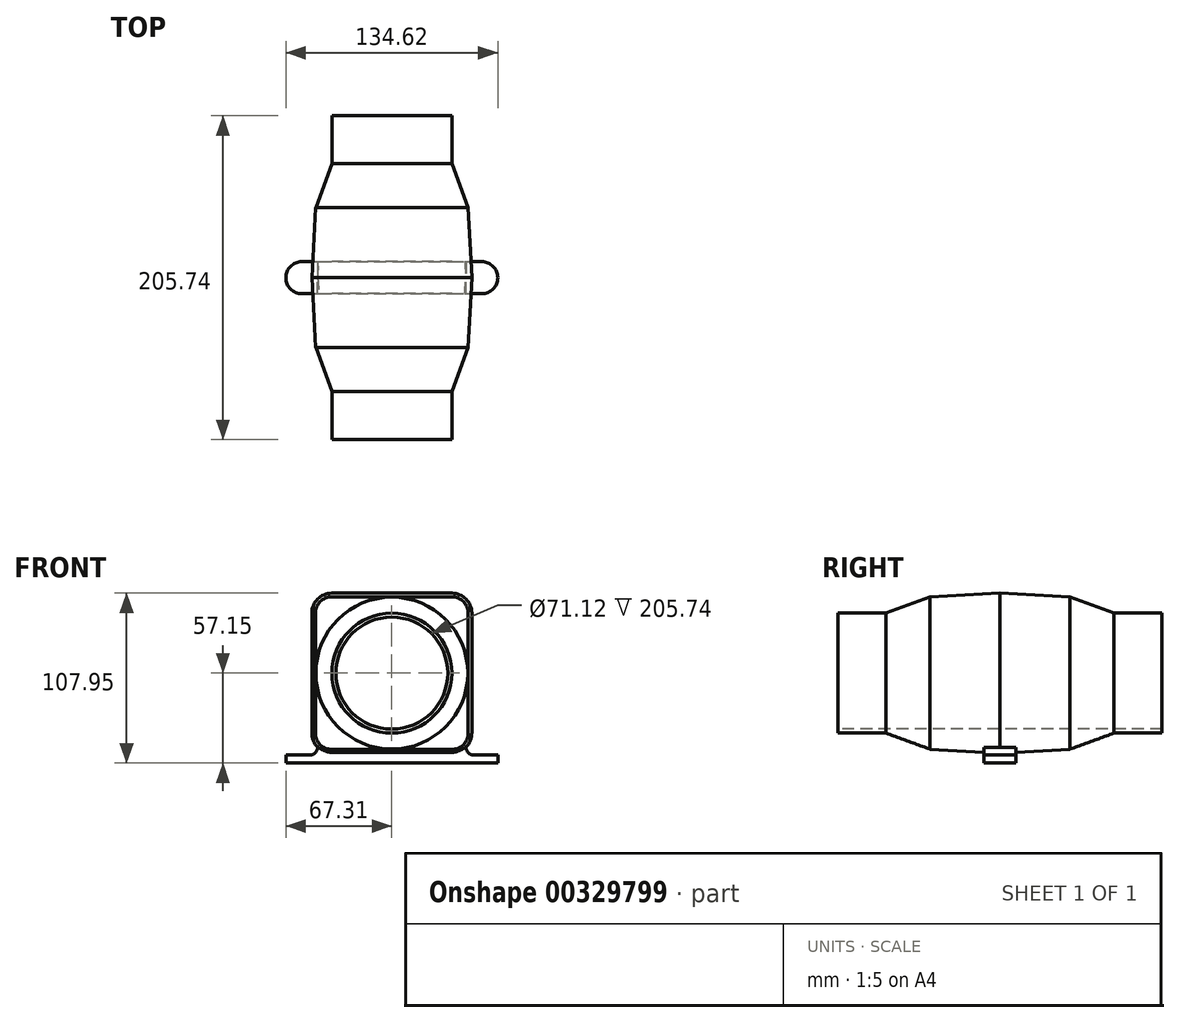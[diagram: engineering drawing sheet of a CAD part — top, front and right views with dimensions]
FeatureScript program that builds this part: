
annotation { "Feature Type Name" : "Feature", "Feature Type Description" : "" }
export const myFeature = defineFeature(function(context is Context, id is Id, definition is map)
    precondition{}
    {
        {
            var Q0;
            Q0=qCreatedBy(makeId("Front.planeOp"),FACE);
            var sketch = newSketch(context, id + "F0", { "sketchPlane" : qUnion([Q0])});
            skLineSegment(sketch, "E0.bottom", {"start": v(38.1, -50.8) * mm, "end": v(-38.1, -50.8) * mm});
            skLineSegment(sketch, "E0.top", {"start": v(38.1, 50.8) * mm, "end": v(-38.1, 50.8) * mm});
            skLineSegment(sketch, "E0.left", {"start": v(50.8, -38.1) * mm, "end": v(50.8, 38.1) * mm});
            skLineSegment(sketch, "E0.right", {"start": v(-50.8, -38.1) * mm, "end": v(-50.8, 38.1) * mm});
            skPoint(sketch, "E0.middle", {"position": v(0, 0) * mm});
            skPoint(sketch, "E1.visualSharp", {"position": v(50.8, 50.8) * mm});
            skArc(sketch, "E1.filletArc", {"start": v(50.8, 38.1) * mm, "mid": v(47.08, 47.08) * mm, "end": v(38.1, 50.8) * mm});
            skPoint(sketch, "E2.visualSharp", {"position": v(-50.8, 50.8) * mm});
            skArc(sketch, "E2.filletArc", {"start": v(-38.1, 50.8) * mm, "mid": v(-47.08, 47.08) * mm, "end": v(-50.8, 38.1) * mm});
            skPoint(sketch, "E3.visualSharp", {"position": v(-50.8, -50.8) * mm});
            skArc(sketch, "E3.filletArc", {"start": v(-50.8, -38.1) * mm, "mid": v(-47.08, -47.08) * mm, "end": v(-38.1, -50.8) * mm});
            skPoint(sketch, "E4.visualSharp", {"position": v(50.8, -50.8) * mm});
            skArc(sketch, "E4.filletArc", {"start": v(38.1, -50.8) * mm, "mid": v(47.08, -47.08) * mm, "end": v(50.8, -38.1) * mm});
            skSolve(sketch);
        }
        {
            var Q0;
            Q0=qSketchRegion(id+"F0",true);
            extrude(context, id + "F1", {"entities" : qUnion([Q0]), "depth" : 44.45 * mm, "hasDraft" : true, "draftAngle" : 3 * degree, "draftPullDirection" : true, "hasSecondDirectionDraft" : true, "secondDirectionDraftAngle" : 3 * degree, "secondDirectionDraftPullDirection" : true});
        }
        {
            var Q0;
            Q0=makeQuery(id+"F1.opExtrude","CAP_FACE",FACE,{"disambiguationData":[OSD([sQuery(id+"F0.wireOp",EDGE,"E0.bottom"),sQuery(id+"F0.wireOp",EDGE,"E0.top"),sQuery(id+"F0.wireOp",EDGE,"E0.left"),sQuery(id+"F0.wireOp",EDGE,"E0.right"),sQuery(id+"F0.wireOp",EDGE,"E1.filletArc"),sQuery(id+"F0.wireOp",EDGE,"E2.filletArc"),sQuery(id+"F0.wireOp",EDGE,"E3.filletArc"),sQuery(id+"F0.wireOp",EDGE,"E4.filletArc")])],"isStart":false});
            var sketch = newSketch(context, id + "F2", { "sketchPlane" : qUnion([Q0])});
            skCircle(sketch, "E5", {"center": v(0, 0) * mm, "radius": 48.26 * mm});
            skSolve(sketch);
        }
        {
            var Q0;
            Q0=qSketchRegion(id+"F2",true);
            extrude(context, id + "F3", {"entities" : qUnion([Q0]), "operationType" : NewBodyOperationType.ADD, "depth" : 27.94 * mm, "hasDraft" : true, "draftAngle" : 20 * degree, "draftPullDirection" : true});
        }
        {
            var Q0;
            Q0=makeQuery(id+"F3.opExtrude","CAP_FACE",FACE,{"disambiguationData":[OSD([sQuery(id+"F2.wireOp",EDGE,"E5")])],"isStart":false});
            var sketch = newSketch(context, id + "F4", { "sketchPlane" : qUnion([Q0])});
            skCircle(sketch, "E6", {"center": v(0, 0) * mm, "radius": 38.1 * mm});
            skSolve(sketch);
        }
        {
            var Q0;
            Q0=qSketchRegion(id+"F4",true);
            extrude(context, id + "F5", {"entities" : qUnion([Q0]), "operationType" : NewBodyOperationType.ADD, "depth" : 30.48 * mm});
        }
        {
            var Q0;
            Q0=qCreatedBy(makeId("Front.planeOp"),FACE);
            var sketch = newSketch(context, id + "F6", { "sketchPlane" : qUnion([Q0])});
            skLineSegment(sketch, "E7.bottom", {"start": v(-67.31, -52.07) * mm, "end": v(-52.16, -52.07) * mm});
            skLineSegment(sketch, "E7.top", {"start": v(-67.31, -57.15) * mm, "end": v(67.31, -57.15) * mm});
            skLineSegment(sketch, "E7.left", {"start": v(-67.31, -52.07) * mm, "end": v(-67.31, -57.15) * mm});
            skLineSegment(sketch, "E7.right", {"start": v(67.3, -52.07) * mm, "end": v(67.31, -57.15) * mm});
            skArc(sketch, "E8", {"start": v(-52.16, -52.07) * mm, "mid": v(-48.6, -50.61) * mm, "end": v(-47.08, -47.08) * mm});
            skArc(sketch, "E9.MirrorCS", {"start": v(52.16, -52.07) * mm, "mid": v(48.6, -50.61) * mm, "end": v(47.08, -47.08) * mm});
            skPoint(sketch, "E10.orphan", {"position": v(-53.69, -51.83) * mm});
            skPoint(sketch, "E11.orphan", {"position": v(53.69, -51.83) * mm});
            skLineSegment(sketch, "E12.trimOffspring", {"start": v(52.16, -52.07) * mm, "end": v(67.3, -52.07) * mm});
            skLineSegment(sketch, "E13", {"start": v(-47.08, -47.08) * mm, "end": v(47.08, -47.08) * mm});
            skSolve(sketch);
        }
        {
            var Q0;
            Q0=qSketchRegion(id+"F6",true);
            extrude(context, id + "F7", {"entities" : qUnion([Q0]), "operationType" : NewBodyOperationType.ADD, "depth" : 10.16 * mm});
        }
        {
            var Q0;
            Q0=makeQuery(id+"F7.opExtrude","CAP_EDGE",EDGE,{"disambiguationData":[OSD([sQuery(id+"F6.wireOp",EDGE,"E7.right")])],"isStart":false});
            var Q1;
            Q1=makeQuery(id+"F7.opExtrude","CAP_EDGE",EDGE,{"disambiguationData":[OSD([sQuery(id+"F6.wireOp",EDGE,"E7.left")])],"isStart":false});
            fillet(context, id + "F8", {"entities" : qUnion([Q0, Q1]), "radius" : 10.16 * mm, "tangentPropagation" : true, "allowEdgeOverflow" : false});
        }
        {
            var Q0;
            Q0=makeQuery(id+"F1.opExtrude","SWEPT_BODY",BODY,{"disambiguationData":[OSD([sQuery(id+"F0.wireOp",EDGE,"E0.bottom"),sQuery(id+"F0.wireOp",EDGE,"E0.top"),sQuery(id+"F0.wireOp",EDGE,"E0.left"),sQuery(id+"F0.wireOp",EDGE,"E0.right"),sQuery(id+"F0.wireOp",EDGE,"E1.filletArc"),sQuery(id+"F0.wireOp",EDGE,"E2.filletArc"),sQuery(id+"F0.wireOp",EDGE,"E3.filletArc"),sQuery(id+"F0.wireOp",EDGE,"E4.filletArc")])]});
            var Q1;
            Q1=qCreatedBy(makeId("Front.planeOp"),FACE);
            mirror(context, id + "F9", {"operationType" : NewBodyOperationType.ADD, "entities" : qUnion([Q0]), "mirrorPlane" : qUnion([Q1])});
        }
        {
            var Q0;
            Q0=makeQuery(id+"F5.opExtrude","CAP_FACE",FACE,{"disambiguationData":[OSD([sQuery(id+"F4.wireOp",EDGE,"E6")])],"isStart":false});
            var sketch = newSketch(context, id + "F10", { "sketchPlane" : qUnion([Q0])});
            skCircle(sketch, "E14", {"center": v(0, 0) * mm, "radius": 35.56 * mm});
            skSolve(sketch);
        }
        {
            var Q0;
            Q0=qSketchRegion(id+"F10",true);
            extrude(context, id + "F11", {"entities" : qUnion([Q0]), "operationType" : NewBodyOperationType.REMOVE, "endBound" : BoundingType.THROUGH_ALL, "oppositeDirection" : true, "depth" : 25.4 * mm});
        }
    });
